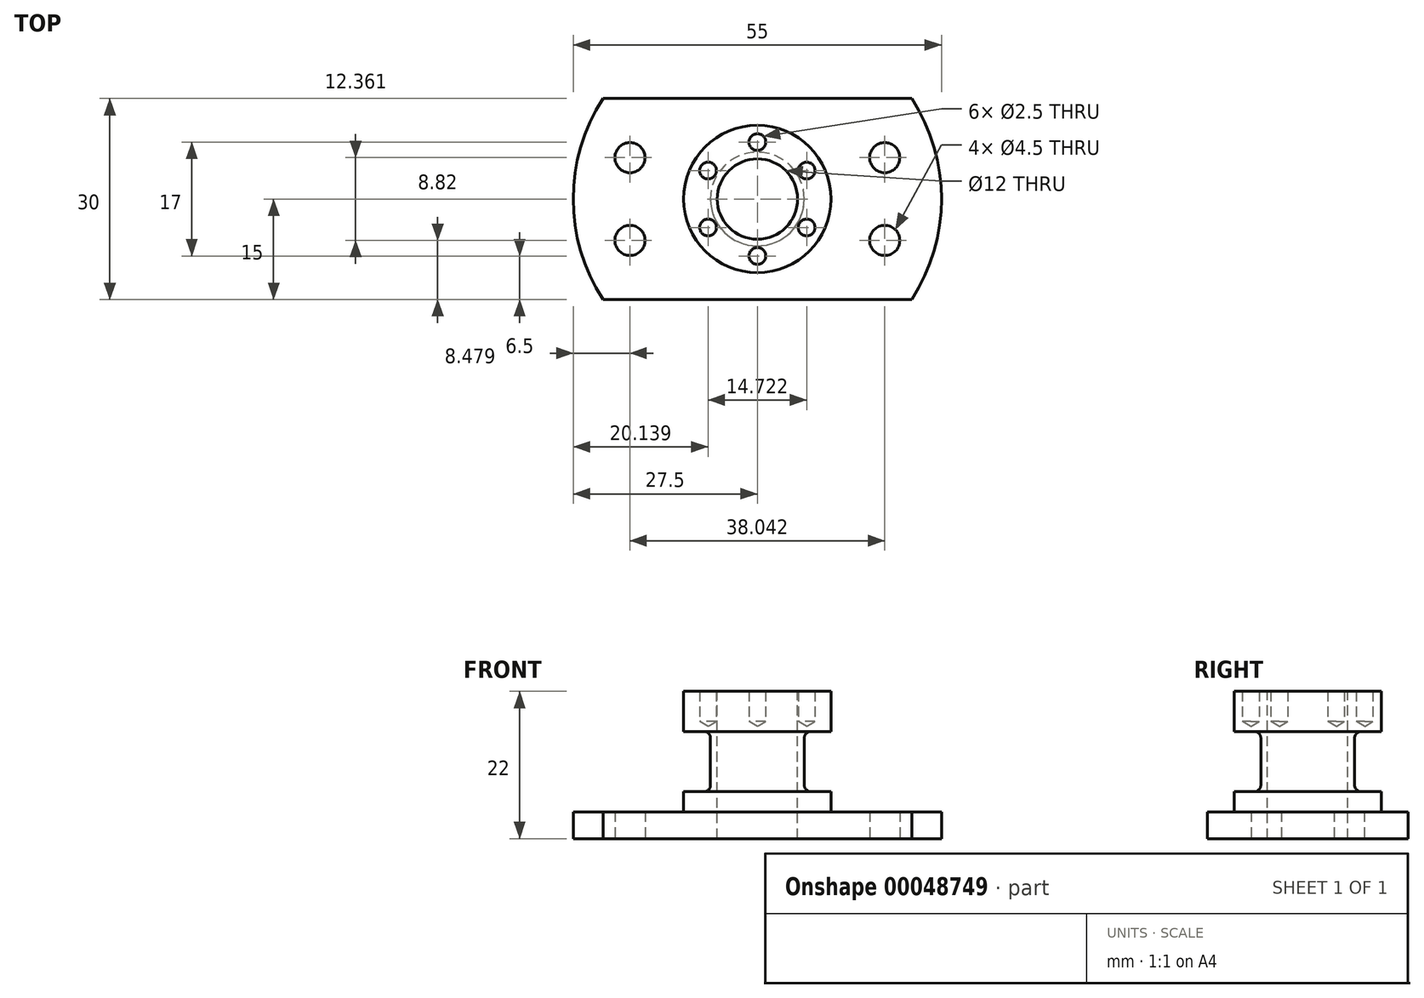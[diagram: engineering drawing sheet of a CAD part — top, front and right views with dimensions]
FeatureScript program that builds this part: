
annotation { "Feature Type Name" : "Feature", "Feature Type Description" : "" }
export const myFeature = defineFeature(function(context is Context, id is Id, definition is map)
    precondition{}
    {
        {
            var Q0;
            Q0=qCreatedBy(makeId("Front.planeOp"),FACE);
            var sketch = newSketch(context, id + "F0", { "sketchPlane" : qUnion([Q0])});
            skLineSegment(sketch, "E0", {"start": v(27.5, 0) * mm, "end": v(27.5, 4) * mm});
            skLineSegment(sketch, "E1", {"start": v(27.5, 4) * mm, "end": v(11, 4) * mm});
            skLineSegment(sketch, "E2", {"start": v(11, 4) * mm, "end": v(11, 7) * mm});
            skLineSegment(sketch, "E3", {"start": v(11, 7) * mm, "end": v(7, 7) * mm});
            skLineSegment(sketch, "E4", {"start": v(7, 7) * mm, "end": v(7, 16) * mm});
            skLineSegment(sketch, "E5", {"start": v(7, 16) * mm, "end": v(11, 16) * mm});
            skLineSegment(sketch, "E6", {"start": v(11, 16) * mm, "end": v(11, 22) * mm});
            skLineSegment(sketch, "E7", {"start": v(11, 22) * mm, "end": v(6, 22) * mm});
            skLineSegment(sketch, "E8", {"start": v(6, 22) * mm, "end": v(6, 0) * mm});
            skLineSegment(sketch, "E9", {"start": v(6, 0) * mm, "end": v(27.5, 0) * mm});
            skLineSegment(sketch, "E10", {"start": v(0, 22.1) * mm, "end": v(0, 0) * mm, "construction": true});
            skSolve(sketch);
        }
        {
            var Q0;
            Q0=makeQuery(id+"F0.imprint","IMPRINT",FACE,{"disambiguationData":[TD([[makeQuery(id+"F0.imprint","IMPRINT",EDGE,{"derivedFrom":sQuery(id+"F0.wireOp",EDGE,"E0")}),1.0]])]});
            var Q1;
            Q1=sQuery(id+"F0.wireOp",EDGE,"E10");
            revolve(context, id + "F1", {"surfaceOperationType" : NewSurfaceOperationType.NEW, "entities" : qUnion([Q0]), "axis" : qUnion([Q1]), "revolveType" : RevolveType.FULL});
        }
        {
            var Q0;
            Q0=makeQuery(id+"F1.opRevolve","SWEPT_EDGE",EDGE,{"disambiguationData":[OSD([sQuery(id+"F0.wireOp",EDGE,"E3"),sQuery(id+"F0.wireOp",EDGE,"E4")])]});
            var Q1;
            Q1=makeQuery(id+"F1.opRevolve","SWEPT_EDGE",EDGE,{"disambiguationData":[OSD([sQuery(id+"F0.wireOp",EDGE,"E4"),sQuery(id+"F0.wireOp",EDGE,"E5")])]});
            fillet(context, id + "F2", {"entities" : qUnion([Q0, Q1]), "tangentPropagation" : true, "radius" : 1 * mm, "defaultsChanged" : false, "vertexSettings" : [], "allowEdgeOverflow" : false});
        }
        {
            var Q0;
            Q0=makeQuery(id+"F1.opRevolve","SWEPT_FACE",FACE,{"disambiguationData":[OSD([sQuery(id+"F0.wireOp",EDGE,"E9")])]});
            var sketch = newSketch(context, id + "F3", { "sketchPlane" : qUnion([Q0])});
            skLineSegment(sketch, "E11.bottom", {"start": v(40, -15) * mm, "end": v(-40, -15) * mm});
            skLineSegment(sketch, "E11.top", {"start": v(40, 15) * mm, "end": v(-40, 15) * mm});
            skLineSegment(sketch, "E11.left", {"start": v(40, -15) * mm, "end": v(40, 15) * mm});
            skLineSegment(sketch, "E11.right", {"start": v(-40, -15) * mm, "end": v(-40, 15) * mm});
            skPoint(sketch, "E11.middle", {"position": v(0, 0) * mm});
            skSolve(sketch);
        }
        {
            var Q0;
            {var subQ0=sQuery(id+"F0.wireOp",EDGE,"E9");Q0=makeQuery(id+"F3.imprint","IMPRINT",FACE,{"disambiguationData":[TD([[makeQuery(id+"F3.imprint","IMPRINT",EDGE,{"derivedFrom":makeQuery(id+"F1.opRevolve","SWEPT_EDGE",EDGE,{"disambiguationData":[OSD([sQuery(id+"F0.wireOp",EDGE,"E8"),subQ0])]})}),1.0]])]});}
            extrude(context, id + "F4", {"entities" : qUnion([Q0]), "operationType" : NewBodyOperationType.INTERSECT, "oppositeDirection" : true, "depth" : 25 * mm, "offsetDistance" : 25 * mm});
        }
        {
            var Q0;
            Q0=makeQuery(id+"F1.opRevolve","SWEPT_FACE",FACE,{"disambiguationData":[OSD([sQuery(id+"F0.wireOp",EDGE,"E7")])]});
            var sketch = newSketch(context, id + "F5", { "sketchPlane" : qUnion([Q0])});
            skPoint(sketch, "E12", {"position": v(0, 8.5) * mm});
            skPoint(sketch, "E13.1.0", {"position": v(-7.36, 4.25) * mm});
            skPoint(sketch, "E13.2.0", {"position": v(-7.36, -4.25) * mm});
            skPoint(sketch, "E13.3.0", {"position": v(0, -8.5) * mm});
            skPoint(sketch, "E13.4.0", {"position": v(7.36, -4.25) * mm});
            skPoint(sketch, "E13.5.0", {"position": v(7.36, 4.25) * mm});
            skPoint(sketch, "E13.center", {"position": v(0, 0) * mm});
            skSolve(sketch);
        }
        {
            var Q0;
            Q0=sQuery(id+"F5.wireOp",VERTEX,"E12");
            var Q1;
            Q1=sQuery(id+"F5.wireOp",VERTEX,"E13.5.0");
            var Q2;
            Q2=sQuery(id+"F5.wireOp",VERTEX,"E13.4.0");
            var Q3;
            Q3=sQuery(id+"F5.wireOp",VERTEX,"E13.3.0");
            var Q4;
            Q4=sQuery(id+"F5.wireOp",VERTEX,"E13.2.0");
            var Q5;
            Q5=sQuery(id+"F5.wireOp",VERTEX,"E13.1.0");
            var Q6;
            Q6=makeQuery(id+"F1.opRevolve","SWEPT_BODY",BODY,{"disambiguationData":[OSD([sQuery(id+"F0.wireOp",EDGE,"E0"),sQuery(id+"F0.wireOp",EDGE,"E1"),sQuery(id+"F0.wireOp",EDGE,"E2"),sQuery(id+"F0.wireOp",EDGE,"E3"),sQuery(id+"F0.wireOp",EDGE,"E4"),sQuery(id+"F0.wireOp",EDGE,"E5"),sQuery(id+"F0.wireOp",EDGE,"E6"),sQuery(id+"F0.wireOp",EDGE,"E7"),sQuery(id+"F0.wireOp",EDGE,"E8"),sQuery(id+"F0.wireOp",EDGE,"E9")])]});
            hole(context, id + "F6", {"style" : HoleStyle.SIMPLE, "endStyle" : HoleEndStyle.BLIND, "standardTappedOrClearance" : lookupTablePath({ "standard" : "ISO", "engagement" : "75%", "pitch" : "0.5 mm", "size" : "M3", "type" : "Tapped" }), "standardBlindInLast" : lookupTablePath({ "standard" : "ISO", "fit" : "Normal", "engagement" : "75%", "pitch" : "0.5 mm", "size" : "M3", "type" : "Clearance & tapped" }), "holeDiameter" : 2.5 * mm, "majorDiameter" : 3 * mm, "showTappedDepth" : true, "holeDepth" : 4.5 * mm, "isTappedThrough" : true, "tappedDepth" : 3 * mm, "tapClearance" : 3, "locations" : qUnion([Q0, Q1, Q2, Q3, Q4, Q5]), "scope" : qUnion([Q6]), "startStyle" : HoleStartStyle.PART});
        }
        {
            var Q0;
            Q0=makeQuery(id+"F1.opRevolve","SWEPT_FACE",FACE,{"disambiguationData":[OSD([sQuery(id+"F0.wireOp",EDGE,"E1")])]});
            var sketch = newSketch(context, id + "F7", { "sketchPlane" : qUnion([Q0])});
            skPoint(sketch, "E14", {"position": v(0, 20) * mm});
            skPoint(sketch, "E15.1.0", {"position": v(-11.76, 16.18) * mm});
            skPoint(sketch, "E15.2.0", {"position": v(-19.02, 6.18) * mm});
            skPoint(sketch, "E15.3.0", {"position": v(-19.02, -6.18) * mm});
            skPoint(sketch, "E15.4.0", {"position": v(-11.76, -16.18) * mm});
            skPoint(sketch, "E15.5.0", {"position": v(0, -20) * mm});
            skPoint(sketch, "E15.6.0", {"position": v(11.76, -16.18) * mm});
            skPoint(sketch, "E15.7.0", {"position": v(19.02, -6.18) * mm});
            skPoint(sketch, "E15.8.0", {"position": v(19.02, 6.18) * mm});
            skPoint(sketch, "E15.9.0", {"position": v(11.76, 16.18) * mm});
            skPoint(sketch, "E15.center", {"position": v(0, 0) * mm});
            skSolve(sketch);
        }
        {
            var Q0;
            Q0=sQuery(id+"F7.wireOp",VERTEX,"E15.2.0");
            var Q1;
            Q1=sQuery(id+"F7.wireOp",VERTEX,"E15.3.0");
            var Q2;
            Q2=sQuery(id+"F7.wireOp",VERTEX,"E15.8.0");
            var Q3;
            Q3=sQuery(id+"F7.wireOp",VERTEX,"E15.7.0");
            var Q4;
            Q4=makeQuery(id+"F1.opRevolve","SWEPT_BODY",BODY,{"disambiguationData":[OSD([sQuery(id+"F0.wireOp",EDGE,"E0"),sQuery(id+"F0.wireOp",EDGE,"E1"),sQuery(id+"F0.wireOp",EDGE,"E2"),sQuery(id+"F0.wireOp",EDGE,"E3"),sQuery(id+"F0.wireOp",EDGE,"E4"),sQuery(id+"F0.wireOp",EDGE,"E5"),sQuery(id+"F0.wireOp",EDGE,"E6"),sQuery(id+"F0.wireOp",EDGE,"E7"),sQuery(id+"F0.wireOp",EDGE,"E8"),sQuery(id+"F0.wireOp",EDGE,"E9")])]});
            hole(context, id + "F8", {"style" : HoleStyle.SIMPLE, "endStyle" : HoleEndStyle.BLIND, "standardTappedOrClearance" : lookupTablePath({ "fit" : "Normal", "standard" : "ISO", "size" : "M4", "type" : "Clearance" }), "standardBlindInLast" : lookupTablePath({ "fit" : "Normal", "standard" : "ISO", "engagement" : "75%", "pitch" : "0.7 mm", "size" : "M4", "type" : "Clearance & tapped" }), "holeDiameter" : 4.5 * mm, "majorDiameter" : 5 * mm, "holeDepth" : 4.5 * mm, "isTappedThrough" : true, "tappedDepth" : 3 * mm, "tapClearance" : 3, "locations" : qUnion([Q0, Q1, Q2, Q3]), "scope" : qUnion([Q4]), "startStyle" : HoleStartStyle.PART});
        }
    });
